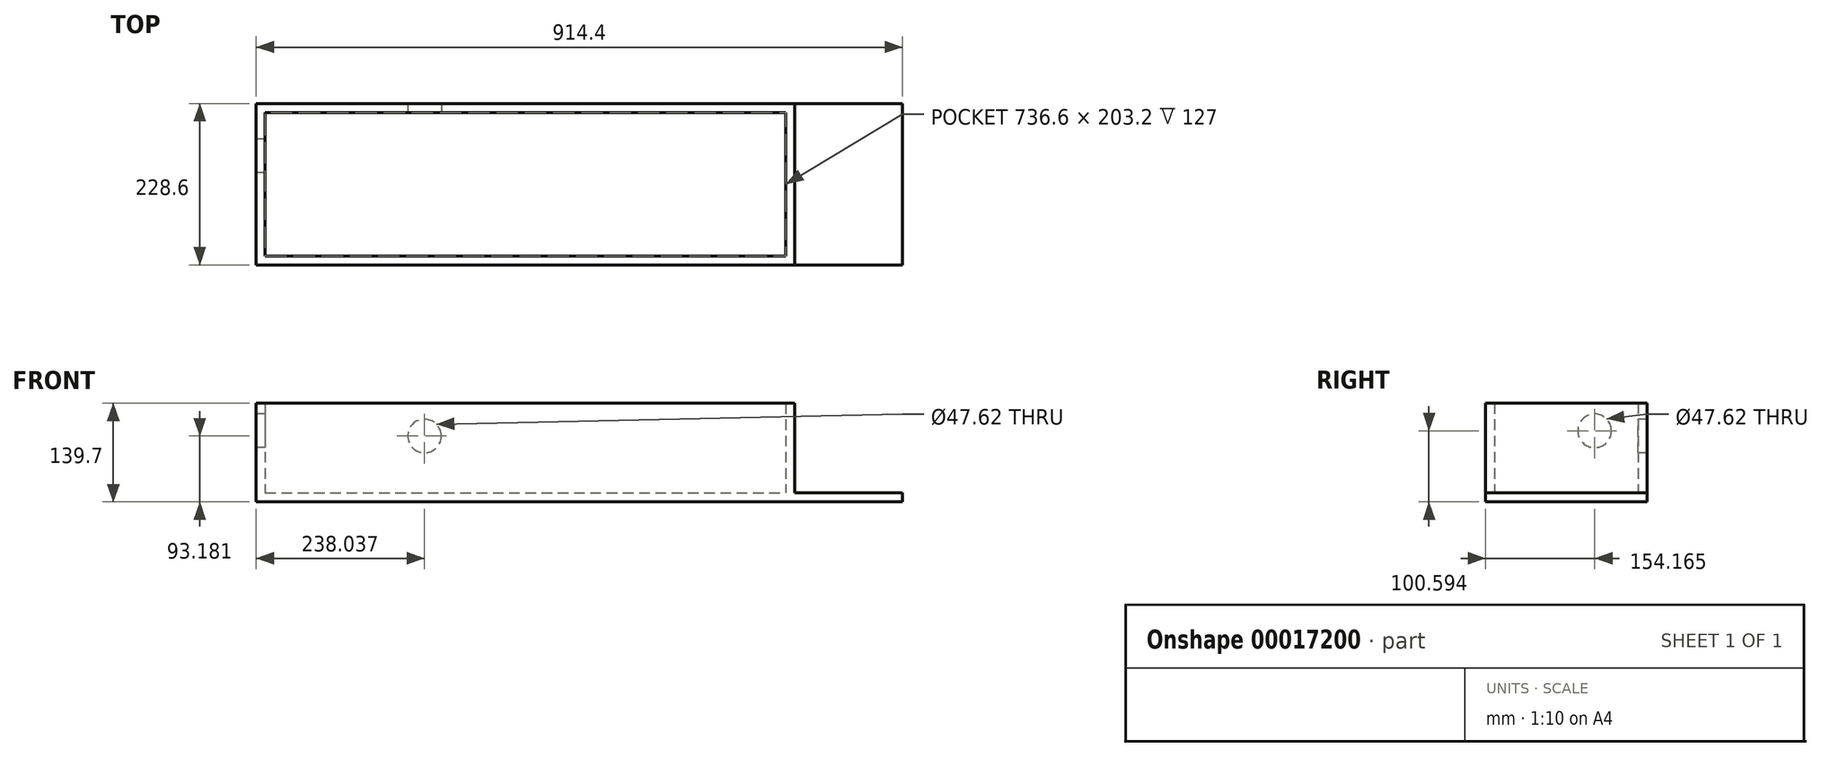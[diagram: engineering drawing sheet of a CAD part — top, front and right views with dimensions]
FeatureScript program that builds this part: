
annotation { "Feature Type Name" : "Feature", "Feature Type Description" : "" }
export const myFeature = defineFeature(function(context is Context, id is Id, definition is map)
    precondition{}
    {
        {
            var Q0;
            Q0=qCreatedBy(makeId("Top.planeOp"),FACE);
            var sketch = newSketch(context, id + "F0", { "sketchPlane" : qUnion([Q0])});
            skLineSegment(sketch, "E0.bottom", {"start": v(0, 0) * mm, "end": v(914.4, 0) * mm});
            skLineSegment(sketch, "E0.top", {"start": v(0, 228.6) * mm, "end": v(914.4, 228.6) * mm});
            skLineSegment(sketch, "E0.left", {"start": v(0, 0) * mm, "end": v(0, 228.6) * mm});
            skLineSegment(sketch, "E0.right", {"start": v(914.4, 0) * mm, "end": v(914.4, 228.6) * mm});
            skSolve(sketch);
        }
        {
            var Q0;
            Q0=qCreatedBy(makeId("Top.planeOp"),FACE);
            var sketch = newSketch(context, id + "F1", { "sketchPlane" : qUnion([Q0])});
            skLineSegment(sketch, "E1.bottom", {"start": v(0, 0) * mm, "end": v(762, 0) * mm});
            skLineSegment(sketch, "E1.top", {"start": v(0, 228.6) * mm, "end": v(762, 228.6) * mm});
            skLineSegment(sketch, "E1.left", {"start": v(0, 0) * mm, "end": v(0, 228.6) * mm});
            skLineSegment(sketch, "E1.right", {"start": v(762, 0) * mm, "end": v(762, 228.6) * mm});
            skSolve(sketch);
        }
        {
            var Q0;
            Q0 = qSketchRegion(id + "F1", true);
            extrude(context, id + "F2", {"entities" : qUnion([Q0]), "depth" : 139.7 * mm});
        }
        {
            var Q0;
            Q0=makeQuery(id+"F0.imprint","IMPRINT",FACE,{"disambiguationData":[TD([[makeQuery(id+"F0.imprint","IMPRINT",EDGE,{"derivedFrom":sQuery(id+"F0.wireOp",EDGE,"E0.bottom")}),1.0]])]});
            extrude(context, id + "F3", {"entities" : qUnion([Q0]), "operationType" : NewBodyOperationType.ADD, "depth" : 12.7 * mm});
        }
        {
            var Q0;
            Q0=makeQuery(id+"F2.opExtrude","CAP_FACE",FACE,{"disambiguationData":[OSD([sQuery(id+"F1.wireOp",EDGE,"E1.bottom"),sQuery(id+"F1.wireOp",EDGE,"E1.top"),sQuery(id+"F1.wireOp",EDGE,"E1.left"),sQuery(id+"F1.wireOp",EDGE,"E1.right")])],"isStart":false});
            shell(context, id + "F4", {"entities" : qUnion([Q0]), "thickness" : 12.7 * mm});
        }
        {
            var Q0;
            Q0=makeQuery(id+"F2.opExtrude","SWEPT_FACE",FACE,{"disambiguationData":[OSD([sQuery(id+"F1.wireOp",EDGE,"E1.left")])]});
            var sketch = newSketch(context, id + "F5", { "sketchPlane" : qUnion([Q0])});
            skCircle(sketch, "E2", {"center": v(-154.16, 100.6) * mm, "radius": 23.81 * mm});
            skSolve(sketch);
        }
        {
            var Q0;
            Q0=sQuery(id+"F5.wireOp",VERTEX,"E2.center");
            var Q1;
            Q1=makeQuery(id+"F2.opExtrude","SWEPT_BODY",BODY,{"disambiguationData":[OSD([sQuery(id+"F1.wireOp",EDGE,"E1.bottom"),sQuery(id+"F1.wireOp",EDGE,"E1.top"),sQuery(id+"F1.wireOp",EDGE,"E1.left"),sQuery(id+"F1.wireOp",EDGE,"E1.right")])]});
            hole(context, id + "F6", {"style" : HoleStyle.SIMPLE, "holeDiameter" : 47.62 * mm, "endStyle" : HoleEndStyle.BLIND, "holeDepth" : 12.7 * mm, "locations" : qUnion([Q0]), "scope" : qUnion([Q1])});
        }
        {
            var Q0;
            Q0=makeQuery(id+"F4.opShell","OFFSET_FACE",FACE,{"disambiguationData":[OSD([sQuery(id+"F0.wireOp",EDGE,"E0.top"),sQuery(id+"F1.wireOp",EDGE,"E1.top")])]});
            var sketch = newSketch(context, id + "F7", { "sketchPlane" : qUnion([Q0])});
            skCircle(sketch, "E3", {"center": v(238.04, 93.18) * mm, "radius": 23.81 * mm});
            skSolve(sketch);
        }
        {
            var Q0;
            Q0=sQuery(id+"F7.wireOp",VERTEX,"E3.center");
            var Q1;
            Q1=makeQuery(id+"F2.opExtrude","SWEPT_BODY",BODY,{"disambiguationData":[OSD([sQuery(id+"F1.wireOp",EDGE,"E1.bottom"),sQuery(id+"F1.wireOp",EDGE,"E1.top"),sQuery(id+"F1.wireOp",EDGE,"E1.left"),sQuery(id+"F1.wireOp",EDGE,"E1.right")])]});
            hole(context, id + "F8", {"style" : HoleStyle.SIMPLE, "holeDiameter" : 47.62 * mm, "endStyle" : HoleEndStyle.BLIND, "holeDepth" : 12.7 * mm, "locations" : qUnion([Q0]), "scope" : qUnion([Q1])});
        }
    });
